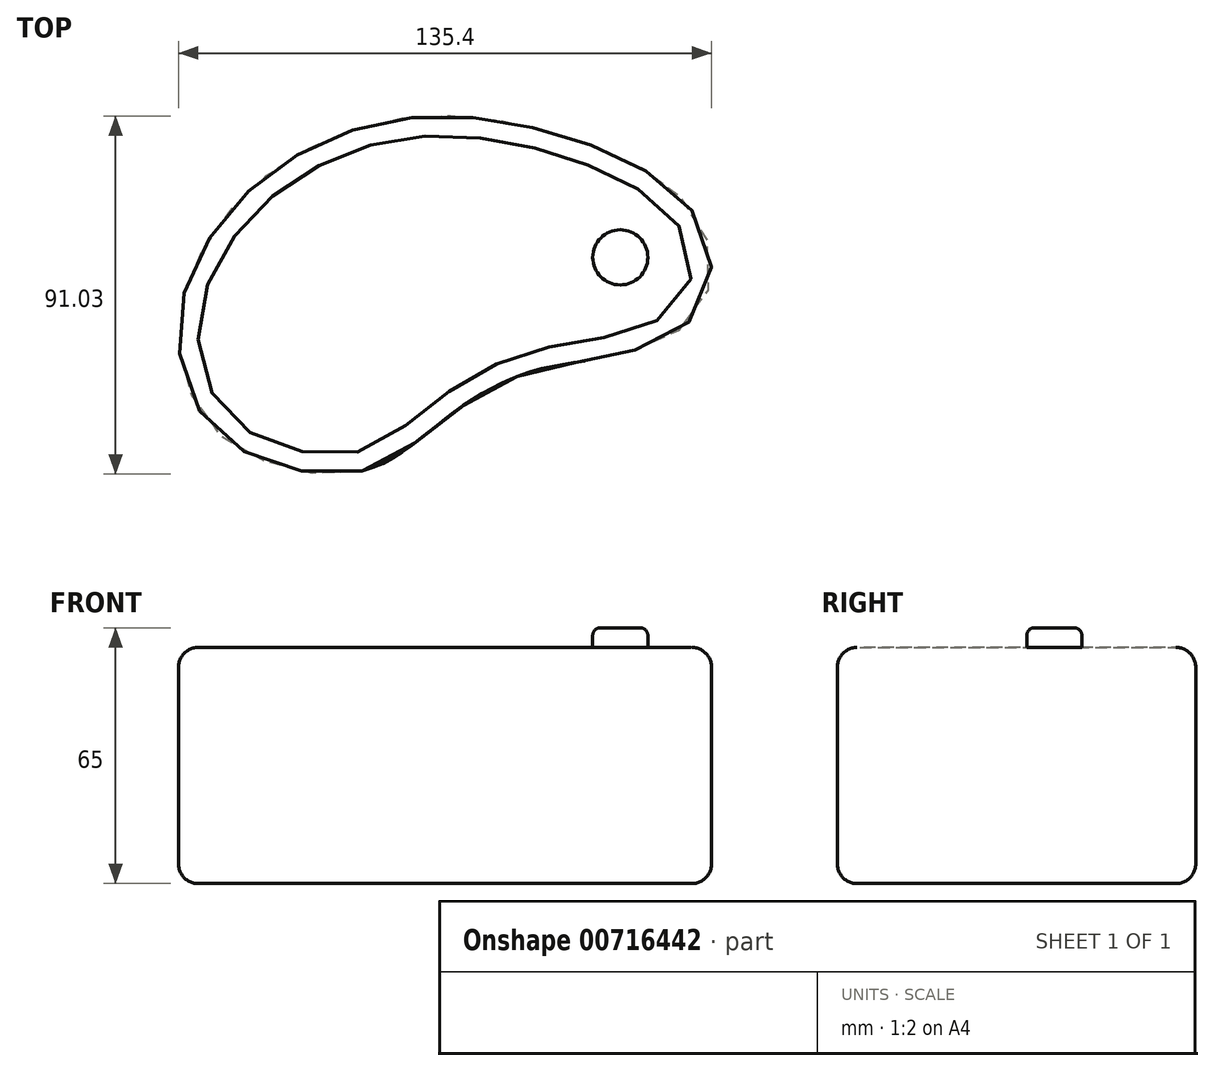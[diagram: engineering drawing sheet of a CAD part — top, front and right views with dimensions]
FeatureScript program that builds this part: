
annotation { "Feature Type Name" : "Feature", "Feature Type Description" : "" }
export const myFeature = defineFeature(function(context is Context, id is Id, definition is map)
    precondition{}
    {
        {
            var Q0;
            Q0=qCreatedBy(makeId("Top.planeOp"),FACE);
            var sketch = newSketch(context, id + "F0", { "sketchPlane" : qUnion([Q0])});
            skLineSegment(sketch, "E0.bottom", {"start": v(0, 0) * mm, "end": v(135, 0) * mm, "construction": true});
            skLineSegment(sketch, "E0.top", {"start": v(0, 90) * mm, "end": v(135, 90) * mm, "construction": true});
            skLineSegment(sketch, "E0.left", {"start": v(0, 0) * mm, "end": v(0, 90) * mm, "construction": true});
            skLineSegment(sketch, "E0.right", {"start": v(135, 0) * mm, "end": v(135, 90) * mm, "construction": true});
            skFitSpline(sketch, "E1", {"points": [v(46.6, 0) * mm, v(18.24, 4.07) * mm, v(5.03, 15.73) * mm, v(0, 32.82) * mm, v(3.48, 51.09) * mm, v(16.3, 69.74) * mm, v(37.67, 84.11) * mm, v(72.25, 90) * mm, v(121.6, 74.4) * mm, v(135, 55.75) * mm, v(130.54, 38.65) * mm, v(108.78, 28.94) * mm, v(88.96, 25.05) * mm, v(68.37, 13.78) * mm, v(46.6, 0) * mm]});
            skSolve(sketch);
        }
        {
            var Q0;
            Q0 = qSketchRegion(id + "F0", true);
            extrude(context, id + "F1", {"entities" : qUnion([Q0]), "depth" : 60 * mm, "offsetDistance" : 25 * mm});
        }
        {
            var Q0;
            Q0=makeQuery(id+"F1.opExtrude","CAP_EDGE",EDGE,{"disambiguationData":[OSD([sQuery(id+"F0.wireOp",EDGE,"E1")])],"isStart":false});
            var Q1;
            Q1=makeQuery(id+"F1.opExtrude","CAP_EDGE",EDGE,{"disambiguationData":[OSD([sQuery(id+"F0.wireOp",EDGE,"E1")])],"isStart":true});
            fillet(context, id + "F2", {"entities" : qUnion([Q0, Q1]), "radius" : 5 * mm, "tangentPropagation" : true, "allowEdgeOverflow" : false});
        }
        {
            var Q0;
            Q0=makeQuery(id+"F1.opExtrude","CAP_FACE",FACE,{"disambiguationData":[OSD([sQuery(id+"F0.wireOp",EDGE,"E1")])],"isStart":false});
            var sketch = newSketch(context, id + "F3", { "sketchPlane" : qUnion([Q0])});
            skCircle(sketch, "E2", {"center": v(112.18, 54.26) * mm, "radius": 7 * mm});
            skSolve(sketch);
        }
        {
            var Q0;
            Q0 = qSketchRegion(id + "F3", true);
            extrude(context, id + "F4", {"entities" : qUnion([Q0]), "operationType" : NewBodyOperationType.ADD, "depth" : 5 * mm, "offsetDistance" : 25 * mm});
        }
        {
            var Q0;
            Q0=makeQuery(id+"F4.opExtrude","CAP_EDGE",EDGE,{"disambiguationData":[OSD([sQuery(id+"F3.wireOp",EDGE,"E2")])],"isStart":false});
            fillet(context, id + "F5", {"entities" : qUnion([Q0]), "radius" : 2 * mm, "tangentPropagation" : true, "allowEdgeOverflow" : false});
        }
    });
